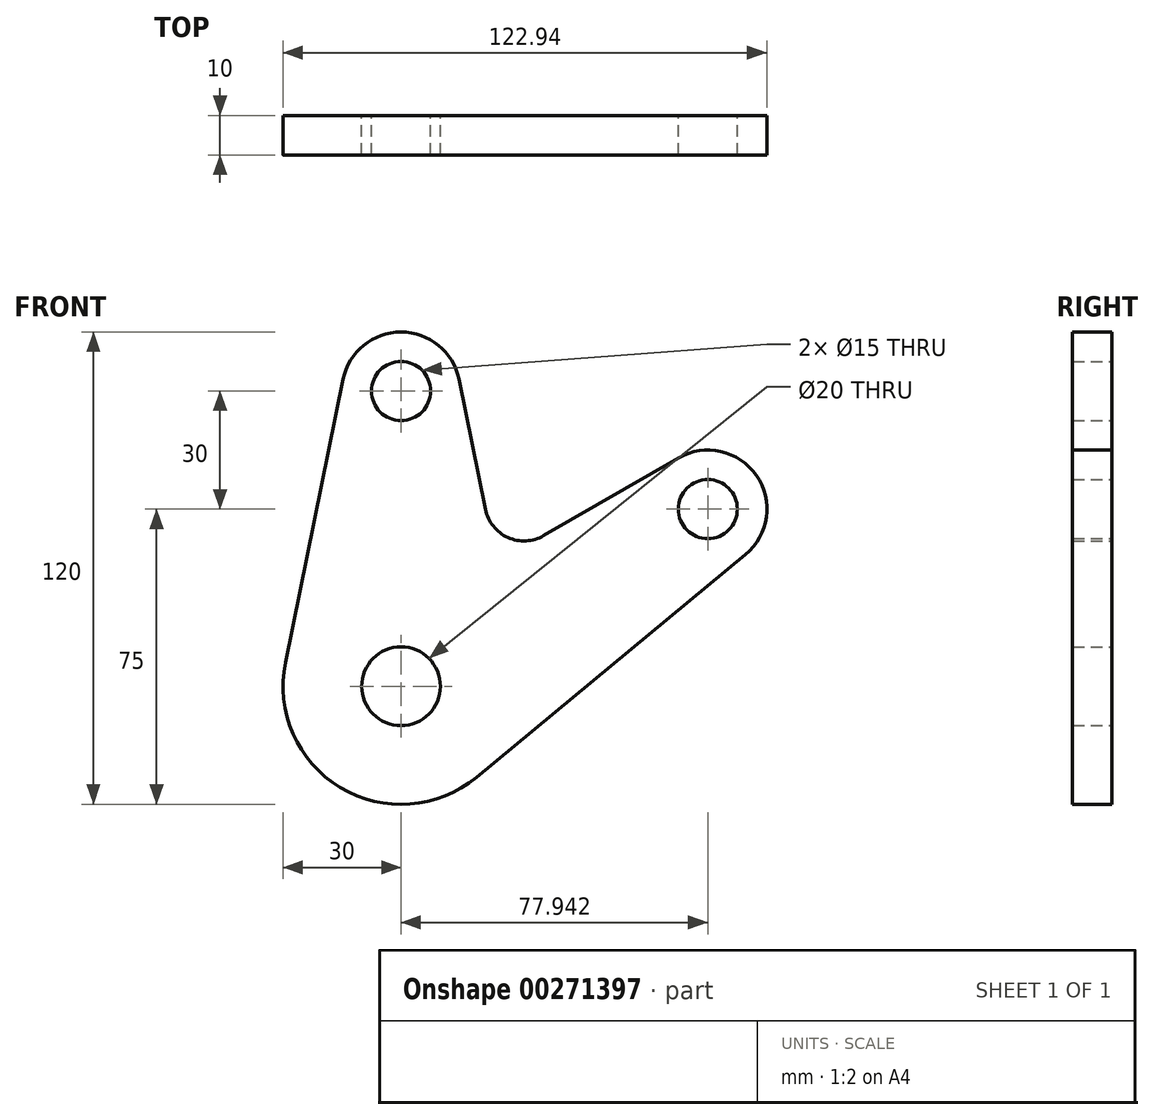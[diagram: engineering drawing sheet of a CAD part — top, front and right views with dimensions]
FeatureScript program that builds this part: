
annotation { "Feature Type Name" : "Feature", "Feature Type Description" : "" }
export const myFeature = defineFeature(function(context is Context, id is Id, definition is map)
    precondition{}
    {
        {
            var Q0;
            Q0=qCreatedBy(makeId("Front.planeOp"),FACE);
            var sketch = newSketch(context, id + "F0", { "sketchPlane" : qUnion([Q0])});
            skCircle(sketch, "E0", {"center": v(0, 0) * mm, "radius": 10 * mm});
            skCircle(sketch, "E1", {"center": v(0, 75) * mm, "radius": 7.5 * mm});
            skCircle(sketch, "E2", {"center": v(77.94, 45) * mm, "radius": 7.5 * mm});
            skArc(sketch, "E3", {"start": v(-29.4, 6) * mm, "mid": v(-15.44, -25.72) * mm, "end": v(19.12, -23.12) * mm});
            skLineSegment(sketch, "E4", {"start": v(-29.4, 6) * mm, "end": v(-14.7, 78) * mm});
            skArc(sketch, "E5", {"start": v(14.7, 78) * mm, "mid": v(0, 90) * mm, "end": v(-14.7, 78) * mm});
            skLineSegment(sketch, "E6", {"start": v(14.7, 78) * mm, "end": v(21.45, 44.9) * mm});
            skArc(sketch, "E7", {"start": v(21.45, 44.9) * mm, "mid": v(27.15, 37.8) * mm, "end": v(36.25, 38.25) * mm});
            skLineSegment(sketch, "E8", {"start": v(87.5, 33.44) * mm, "end": v(19.12, -23.12) * mm});
            skLineSegment(sketch, "E9", {"start": v(0, 0) * mm, "end": v(0, 75) * mm, "construction": true});
            skLineSegment(sketch, "E10", {"start": v(0, 0) * mm, "end": v(77.94, 45) * mm, "construction": true});
            skArc(sketch, "E11", {"start": v(87.5, 33.44) * mm, "mid": v(90.26, 53.56) * mm, "end": v(70.44, 58) * mm});
            skLineSegment(sketch, "E12", {"start": v(70.44, 58) * mm, "end": v(36.25, 38.25) * mm});
            skSolve(sketch);
        }
        {
            var Q0;
            Q0 = qSketchRegion(id + "F0", true);
            extrude(context, id + "F1", {"entities" : qUnion([Q0]), "depth" : 10 * mm});
        }
    });
